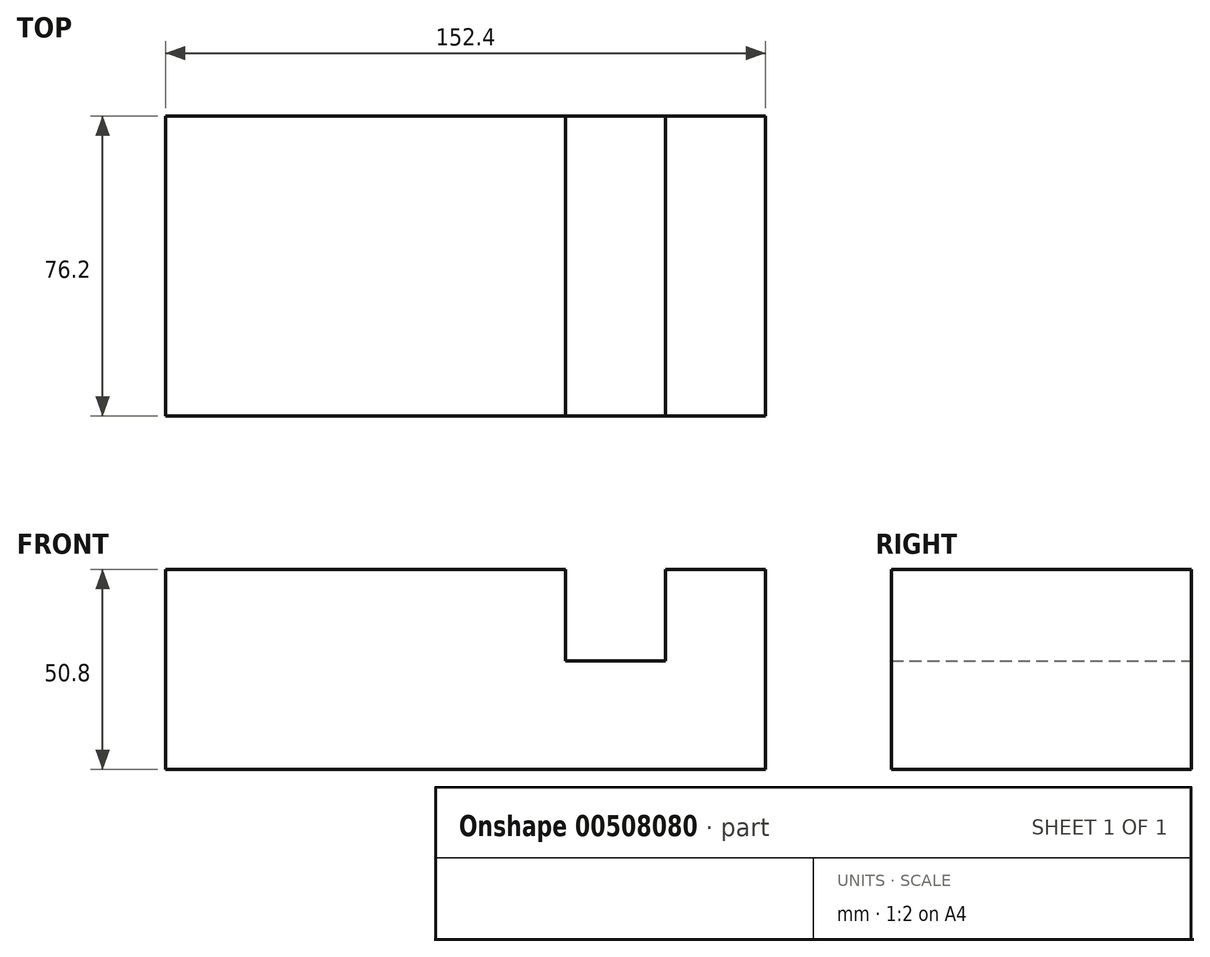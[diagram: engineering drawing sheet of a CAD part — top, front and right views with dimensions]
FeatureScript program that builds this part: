
annotation { "Feature Type Name" : "Feature", "Feature Type Description" : "" }
export const myFeature = defineFeature(function(context is Context, id is Id, definition is map)
    precondition{}
    {
        {
            var Q0;
            Q0=qCreatedBy(makeId("Front.planeOp"),FACE);
            var sketch = newSketch(context, id + "F0", { "sketchPlane" : qUnion([Q0])});
            skLineSegment(sketch, "E0", {"start": v(-96.48, 52.7) * mm, "end": v(5.12, 52.7) * mm});
            skLineSegment(sketch, "E1", {"start": v(5.12, 52.7) * mm, "end": v(5.12, 29.42) * mm});
            skLineSegment(sketch, "E2", {"start": v(5.12, 29.42) * mm, "end": v(30.52, 29.42) * mm});
            skLineSegment(sketch, "E3", {"start": v(30.52, 29.42) * mm, "end": v(30.52, 52.7) * mm});
            skLineSegment(sketch, "E4", {"start": v(30.52, 52.7) * mm, "end": v(55.92, 52.7) * mm});
            skLineSegment(sketch, "E5", {"start": v(55.92, 52.7) * mm, "end": v(55.92, 1.9) * mm});
            skLineSegment(sketch, "E6", {"start": v(55.92, 1.9) * mm, "end": v(-96.48, 1.9) * mm});
            skLineSegment(sketch, "E7", {"start": v(-96.48, 1.9) * mm, "end": v(-96.48, 52.7) * mm});
            skSolve(sketch);
        }
        {
            var Q0;
            Q0 = qSketchRegion(id + "F0", true);
            extrude(context, id + "F1", {"entities" : qUnion([Q0]), "depth" : 76.2 * mm});
        }
    });
